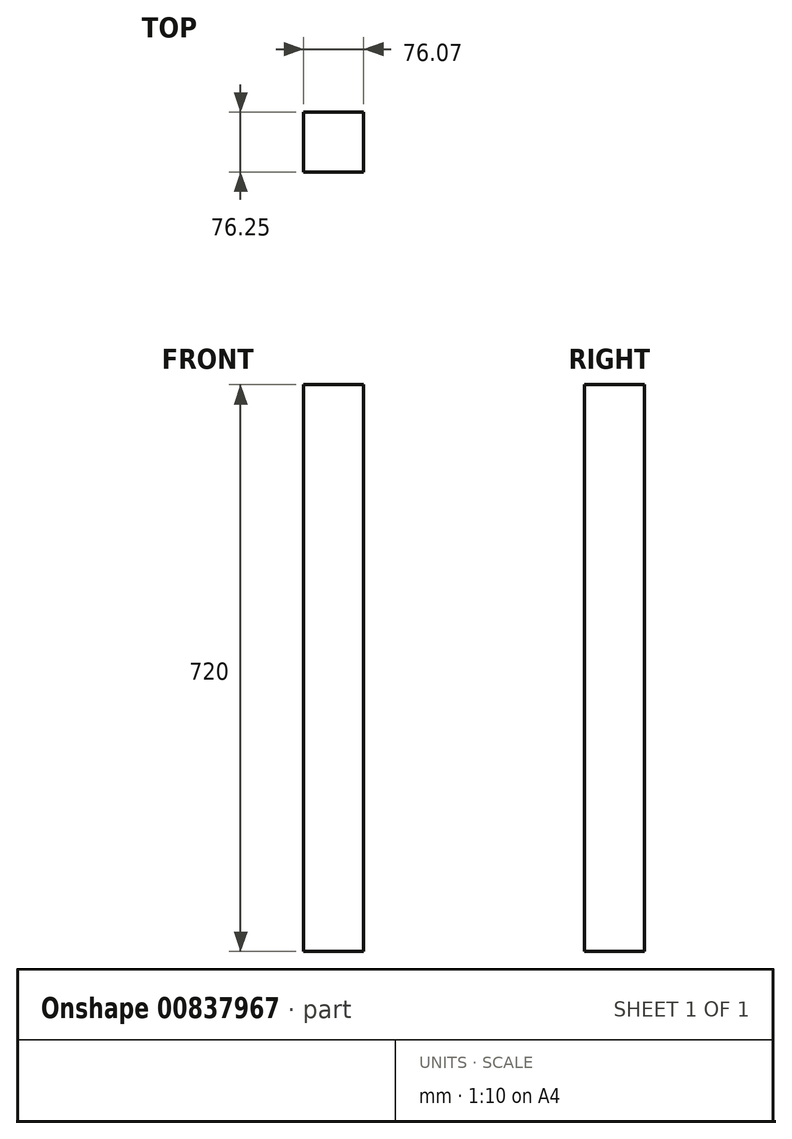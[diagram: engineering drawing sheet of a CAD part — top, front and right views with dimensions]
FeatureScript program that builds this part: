
annotation { "Feature Type Name" : "Feature", "Feature Type Description" : "" }
export const myFeature = defineFeature(function(context is Context, id is Id, definition is map)
    precondition{}
    {
        {
            var Q0;
            Q0=qCreatedBy(makeId("Top.planeOp"),FACE);
            var sketch = newSketch(context, id + "F0", { "sketchPlane" : qUnion([Q0])});
            skLineSegment(sketch, "E0.bottom", {"start": v(-76.07, 0) * mm, "end": v(0, 0) * mm});
            skLineSegment(sketch, "E0.top", {"start": v(-76.07, -76.25) * mm, "end": v(0, -76.25) * mm});
            skLineSegment(sketch, "E0.left", {"start": v(-76.07, 0) * mm, "end": v(-76.07, -76.25) * mm});
            skLineSegment(sketch, "E0.right", {"start": v(0, 0) * mm, "end": v(0, -76.25) * mm});
            skSolve(sketch);
        }
        {
            var Q0;
            Q0=makeQuery(id+"F0.imprint","IMPRINT",FACE,{"disambiguationData":[TD([[makeQuery(id+"F0.imprint","IMPRINT",EDGE,{"derivedFrom":sQuery(id+"F0.wireOp",EDGE,"E0.bottom")}),-1.0]])]});
            var sketch = newSketch(context, id + "F1", { "sketchPlane" : qUnion([Q0])});
            skSolve(sketch);
        }
        {
            var Q0;
            Q0=makeQuery(id+"F1.imprint","IMPRINT",FACE,{"disambiguationData":[TD([[makeQuery(id+"F1.imprint","IMPRINT",EDGE,{"derivedFrom":makeQuery(id+"F0.imprint","IMPRINT",EDGE,{"derivedFrom":sQuery(id+"F0.wireOp",EDGE,"E0.bottom")})}),-1.0]])]});
            extrude(context, id + "F2", {"entities" : qUnion([Q0]), "depth" : 720 * mm, "offsetDistance" : 25.4 * mm});
        }
    });
